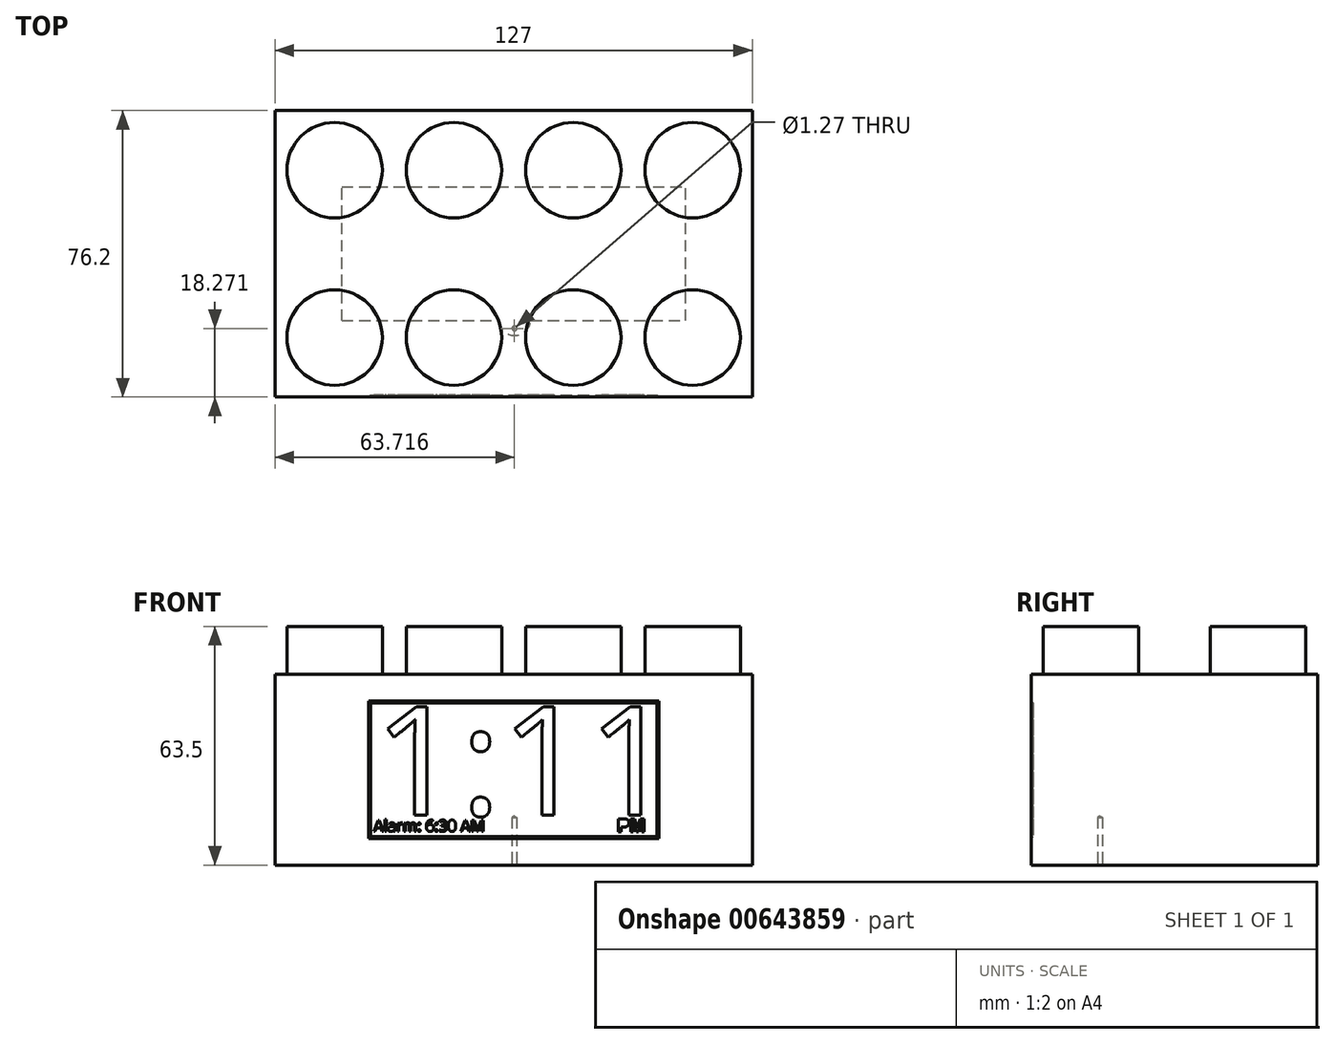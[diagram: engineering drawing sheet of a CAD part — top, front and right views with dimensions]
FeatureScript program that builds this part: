
annotation { "Feature Type Name" : "Feature", "Feature Type Description" : "" }
export const myFeature = defineFeature(function(context is Context, id is Id, definition is map)
    precondition{}
    {
        {
            var Q0;
            Q0=qCreatedBy(makeId("Top.planeOp"),FACE);
            var sketch = newSketch(context, id + "F0", { "sketchPlane" : qUnion([Q0])});
            skLineSegment(sketch, "E0.bottom", {"start": v(63.5, 38.1) * mm, "end": v(-63.5, 38.1) * mm});
            skLineSegment(sketch, "E0.top", {"start": v(63.5, -38.1) * mm, "end": v(-63.5, -38.1) * mm});
            skLineSegment(sketch, "E0.left", {"start": v(63.5, 38.1) * mm, "end": v(63.5, -38.1) * mm});
            skLineSegment(sketch, "E0.right", {"start": v(-63.5, 38.1) * mm, "end": v(-63.5, -38.1) * mm});
            skPoint(sketch, "E0.middle", {"position": v(0, 0) * mm});
            skSolve(sketch);
        }
        {
            var Q0;
            Q0 = qSketchRegion(id + "F0", true);
            extrude(context, id + "F1", {"entities" : qUnion([Q0]), "depth" : 50.8 * mm, "offsetDistance" : 25.4 * mm});
        }
        {
            var Q0;
            Q0=makeQuery(id+"F1.opExtrude","CAP_FACE",FACE,{"disambiguationData":[OSD([sQuery(id+"F0.wireOp",EDGE,"E0.bottom"),sQuery(id+"F0.wireOp",EDGE,"E0.top"),sQuery(id+"F0.wireOp",EDGE,"E0.left"),sQuery(id+"F0.wireOp",EDGE,"E0.right")])],"isStart":false});
            var sketch = newSketch(context, id + "F2", { "sketchPlane" : qUnion([Q0])});
            skCircle(sketch, "E1", {"center": v(-47.65, 22.25) * mm, "radius": 12.7 * mm});
            skCircle(sketch, "E2", {"center": v(-15.9, 22.25) * mm, "radius": 12.7 * mm});
            skCircle(sketch, "E3", {"center": v(15.85, 22.25) * mm, "radius": 12.7 * mm});
            skCircle(sketch, "E4", {"center": v(47.6, 22.25) * mm, "radius": 12.7 * mm});
            skCircle(sketch, "E5", {"center": v(-47.65, -22.25) * mm, "radius": 12.7 * mm});
            skCircle(sketch, "E6", {"center": v(-15.9, -22.25) * mm, "radius": 12.7 * mm});
            skCircle(sketch, "E7", {"center": v(15.85, -22.25) * mm, "radius": 12.7 * mm});
            skCircle(sketch, "E8", {"center": v(47.6, -22.25) * mm, "radius": 12.7 * mm});
            skSolve(sketch);
        }
        {
            var Q0;
            Q0=makeQuery(id+"F2.imprint","IMPRINT",FACE,{"disambiguationData":[TD([[makeQuery(id+"F2.imprint","IMPRINT",EDGE,{"derivedFrom":sQuery(id+"F2.wireOp",EDGE,"E1")}),1.0]])]});
            var Q1;
            Q1=makeQuery(id+"F2.imprint","IMPRINT",FACE,{"disambiguationData":[TD([[makeQuery(id+"F2.imprint","IMPRINT",EDGE,{"derivedFrom":sQuery(id+"F2.wireOp",EDGE,"E5")}),1.0]])]});
            var Q2;
            Q2=makeQuery(id+"F2.imprint","IMPRINT",FACE,{"disambiguationData":[TD([[makeQuery(id+"F2.imprint","IMPRINT",EDGE,{"derivedFrom":sQuery(id+"F2.wireOp",EDGE,"E6")}),1.0]])]});
            var Q3;
            Q3=makeQuery(id+"F2.imprint","IMPRINT",FACE,{"disambiguationData":[TD([[makeQuery(id+"F2.imprint","IMPRINT",EDGE,{"derivedFrom":sQuery(id+"F2.wireOp",EDGE,"E2")}),1.0]])]});
            var Q4;
            Q4=makeQuery(id+"F2.imprint","IMPRINT",FACE,{"disambiguationData":[TD([[makeQuery(id+"F2.imprint","IMPRINT",EDGE,{"derivedFrom":sQuery(id+"F2.wireOp",EDGE,"E3")}),1.0]])]});
            var Q5;
            Q5=makeQuery(id+"F2.imprint","IMPRINT",FACE,{"disambiguationData":[TD([[makeQuery(id+"F2.imprint","IMPRINT",EDGE,{"derivedFrom":sQuery(id+"F2.wireOp",EDGE,"E4")}),1.0]])]});
            var Q6;
            Q6=makeQuery(id+"F2.imprint","IMPRINT",FACE,{"disambiguationData":[TD([[makeQuery(id+"F2.imprint","IMPRINT",EDGE,{"derivedFrom":sQuery(id+"F2.wireOp",EDGE,"E8")}),1.0]])]});
            var Q7;
            Q7=makeQuery(id+"F2.imprint","IMPRINT",FACE,{"disambiguationData":[TD([[makeQuery(id+"F2.imprint","IMPRINT",EDGE,{"derivedFrom":sQuery(id+"F2.wireOp",EDGE,"E7")}),1.0]])]});
            extrude(context, id + "F3", {"entities" : qUnion([Q0, Q1, Q2, Q3, Q4, Q5, Q6, Q7]), "operationType" : NewBodyOperationType.ADD, "depth" : 12.7 * mm, "offsetDistance" : 25.4 * mm});
        }
        {
            var Q0;
            Q0=makeQuery(id+"F1.opExtrude","SWEPT_FACE",FACE,{"disambiguationData":[OSD([sQuery(id+"F0.wireOp",EDGE,"E0.top")])]});
            var sketch = newSketch(context, id + "F4", { "sketchPlane" : qUnion([Q0])});
            skLineSegment(sketch, "E9.bottom", {"start": v(-38.1, 43.18) * mm, "end": v(38.1, 43.18) * mm});
            skLineSegment(sketch, "E9.top", {"start": v(-38.1, 7.62) * mm, "end": v(38.1, 7.62) * mm});
            skLineSegment(sketch, "E9.left", {"start": v(-38.1, 43.18) * mm, "end": v(-38.1, 7.62) * mm});
            skLineSegment(sketch, "E9.right", {"start": v(38.1, 43.18) * mm, "end": v(38.1, 7.62) * mm});
            skText(sketch, "E10", { "text": "1:11", "fontName": "OpenSans-Regular.ttf"});
            skText(sketch, "E11", { "text": "Alarm: 6:30 AM", "fontName": "OpenSans-Regular.ttf"});
            skText(sketch, "E12", { "text": "PM", "fontName": "Arimo-Bold.ttf"});
            const initialGuessF4  = {"E10": [-0.03724, 0.01331, 1, 0, 0.0291], "E11": [-0.03724, 0.00897, 1, 0, 0.003], "E12": [0.0275, 0.0089, 1, 0, 0.00359]};
            skSetInitialGuess(sketch, initialGuessF4);
            skSolve(sketch);
        }
        {
            var Q0;
            Q0=makeQuery(id+"F4.imprint","IMPRINT",FACE,{"disambiguationData":[TD([[makeQuery(id+"F4.imprint","IMPRINT",EDGE,{"derivedFrom":sQuery(id+"F4.wireOp",EDGE,"E9.bottom")}),-1.0]])]});
            extrude(context, id + "F5", {"entities" : qUnion([Q0]), "operationType" : NewBodyOperationType.REMOVE, "oppositeDirection" : true, "depth" : 0.5 * mm, "offsetDistance" : 25.4 * mm});
        }
        {
            var Q0;
            Q0=makeQuery(id+"F5.boolean.opBoolean","COPY",EDGE,{"derivedFrom":makeQuery(id+"F5.opExtrude","CAP_EDGE",EDGE,{"disambiguationData":[OSD([sQuery(id+"F4.wireOp",EDGE,"E9.left")])],"isStart":true})});
            var Q1;
            Q1=makeQuery(id+"F5.boolean.opBoolean","COPY",EDGE,{"derivedFrom":makeQuery(id+"F5.opExtrude","CAP_EDGE",EDGE,{"disambiguationData":[OSD([sQuery(id+"F4.wireOp",EDGE,"E9.bottom")])],"isStart":true})});
            var Q2;
            Q2=makeQuery(id+"F5.boolean.opBoolean","COPY",EDGE,{"derivedFrom":makeQuery(id+"F5.opExtrude","CAP_EDGE",EDGE,{"disambiguationData":[OSD([sQuery(id+"F4.wireOp",EDGE,"E9.right")])],"isStart":true})});
            var Q3;
            Q3=makeQuery(id+"F5.boolean.opBoolean","COPY",EDGE,{"derivedFrom":makeQuery(id+"F5.opExtrude","CAP_EDGE",EDGE,{"disambiguationData":[OSD([sQuery(id+"F4.wireOp",EDGE,"E9.top")])],"isStart":true})});
            chamfer(context, id + "F6", {"entities" : qUnion([Q0, Q1, Q2, Q3]), "width" : 0.5 * mm, "tangentPropagation" : true});
        }
        {
            var Q0;
            Q0=makeQuery(id+"F0.imprint","IMPRINT",FACE,{"disambiguationData":[TD([[makeQuery(id+"F0.imprint","IMPRINT",EDGE,{"derivedFrom":sQuery(id+"F0.wireOp",EDGE,"E0.bottom")}),1.0]])]});
            var sketch = newSketch(context, id + "F7", { "sketchPlane" : qUnion([Q0])});
            skLineSegment(sketch, "E13.bottom", {"start": v(-45.72, -17.78) * mm, "end": v(45.72, -17.78) * mm});
            skLineSegment(sketch, "E13.top", {"start": v(-45.72, 17.78) * mm, "end": v(45.72, 17.78) * mm});
            skLineSegment(sketch, "E13.left", {"start": v(-45.72, -17.78) * mm, "end": v(-45.72, 17.78) * mm});
            skLineSegment(sketch, "E13.right", {"start": v(45.72, -17.78) * mm, "end": v(45.72, 17.78) * mm});
            skPoint(sketch, "E13.middle", {"position": v(0, 0) * mm});
            skArc(sketch, "E14", {"start": v(-4.05, -17.78) * mm, "mid": v(0.22, -21.73) * mm, "end": v(4.48, -17.78) * mm});
            skPoint(sketch, "E15", {"position": v(0.22, -19.83) * mm});
            skSolve(sketch);
        }
        {
            var Q0;
            Q0=sQuery(id+"F7.wireOp",VERTEX,"E15");
            var Q1;
            Q1=makeQuery(id+"F1.opExtrude","SWEPT_BODY",BODY,{"disambiguationData":[OSD([sQuery(id+"F0.wireOp",EDGE,"E0.bottom"),sQuery(id+"F0.wireOp",EDGE,"E0.top"),sQuery(id+"F0.wireOp",EDGE,"E0.left"),sQuery(id+"F0.wireOp",EDGE,"E0.right")])]});
            hole(context, id + "F8", {"style" : HoleStyle.C_SINK, "endStyle" : HoleEndStyle.BLIND, "oppositeDirection" : true, "holeDiameter" : 1.27 * mm, "cSinkDiameter" : 1.27 * mm, "cSinkAngle" : 85 * degree, "majorDiameter" : 6.35 * mm, "holeDepth" : 12.7 * mm, "tappedDepth" : 10.8 * mm, "tapClearance" : 3, "startFromSketch" : true, "locations" : qUnion([Q0]), "scope" : qUnion([Q1])});
        }
        {
            var Q0;
            Q0 = qSketchRegion(id + "F7", true);
            extrude(context, id + "F9", {"entities" : qUnion([Q0]), "operationType" : NewBodyOperationType.REMOVE, "depth" : 0.13 * mm, "offsetDistance" : 25.4 * mm});
        }
    });
